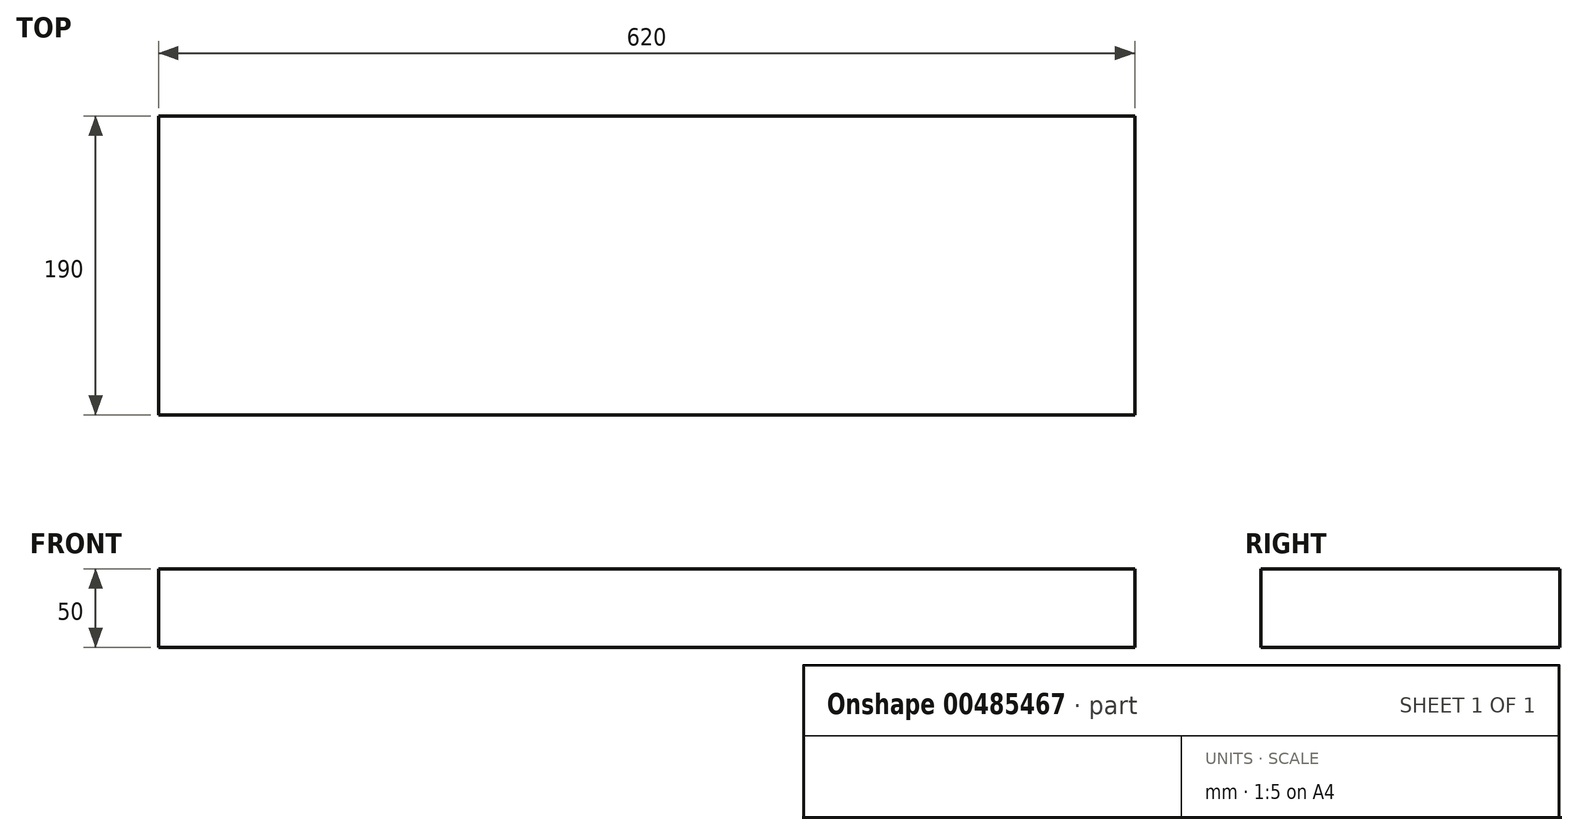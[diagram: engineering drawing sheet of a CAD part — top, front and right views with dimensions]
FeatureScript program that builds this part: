
annotation { "Feature Type Name" : "Feature", "Feature Type Description" : "" }
export const myFeature = defineFeature(function(context is Context, id is Id, definition is map)
    precondition{}
    {
        {
            var Q0;
            Q0=qCreatedBy(makeId("Top.planeOp"),FACE);
            var sketch = newSketch(context, id + "F0", { "sketchPlane" : qUnion([Q0])});
            skLineSegment(sketch, "E0.bottom", {"start": v(-509.87, -280.53) * mm, "end": v(110.13, -280.53) * mm});
            skLineSegment(sketch, "E0.top", {"start": v(-509.87, -90.53) * mm, "end": v(110.13, -90.53) * mm});
            skLineSegment(sketch, "E0.left", {"start": v(-509.87, -280.53) * mm, "end": v(-509.87, -90.53) * mm});
            skLineSegment(sketch, "E0.right", {"start": v(110.13, -280.53) * mm, "end": v(110.13, -90.53) * mm});
            skSolve(sketch);
        }
        {
            var Q0;
            Q0=qSketchRegion(id+"F0",true);
            extrude(context, id + "F1", {"entities" : qUnion([Q0]), "depth" : 50 * mm});
        }
    });
